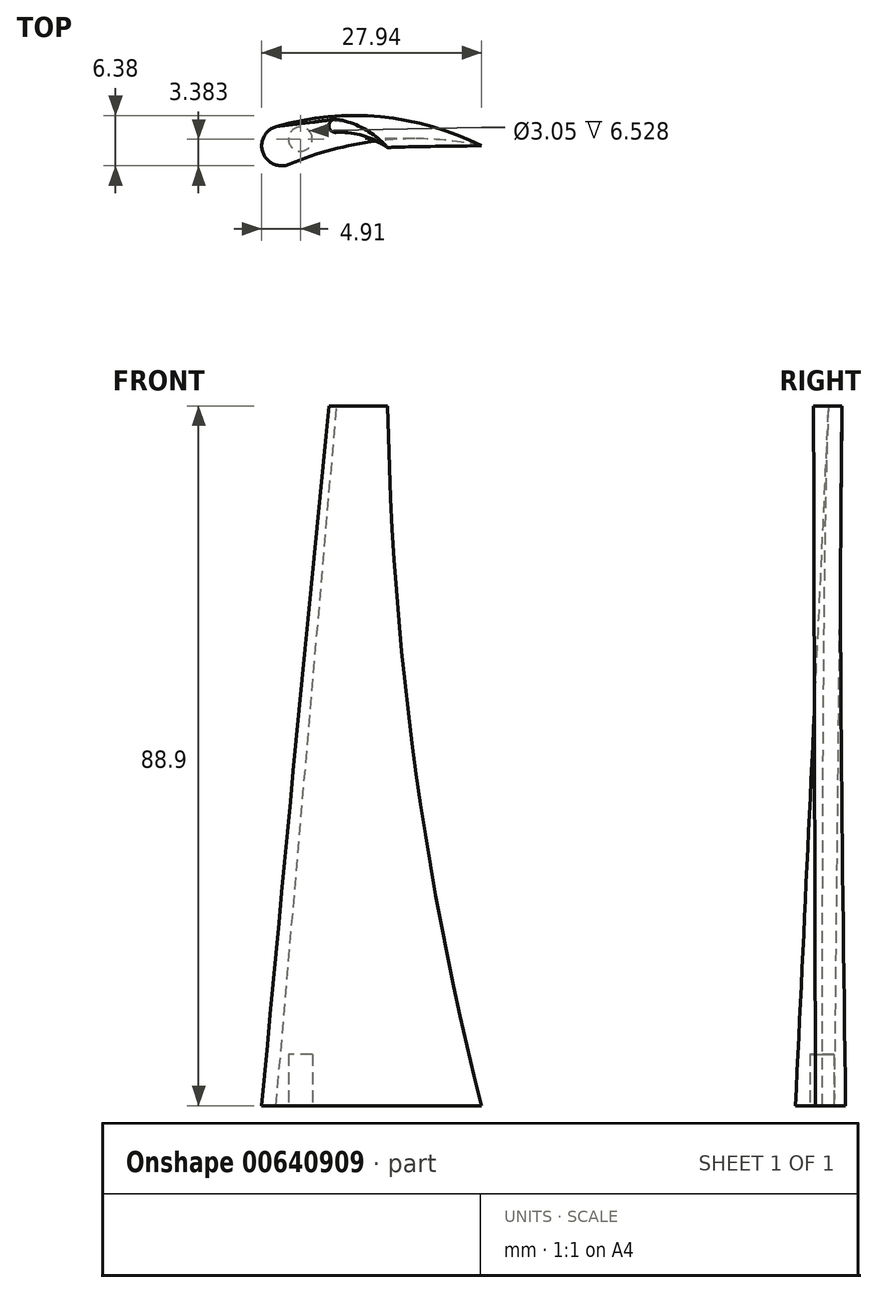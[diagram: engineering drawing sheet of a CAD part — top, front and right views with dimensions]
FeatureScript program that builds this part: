
annotation { "Feature Type Name" : "Feature", "Feature Type Description" : "" }
export const myFeature = defineFeature(function(context is Context, id is Id, definition is map)
    precondition{}
    {
        {
            var Q0;
            Q0=qCreatedBy(makeId("Top.planeOp"),FACE);
            var sketch = newSketch(context, id + "F0", { "sketchPlane" : qUnion([Q0])});
            skLineSegment(sketch, "E0", {"start": v(0, 0) * mm, "end": v(25.4, 0) * mm, "construction": true});
            skArc(sketch, "E1", {"start": v(25.4, 0) * mm, "mid": v(12.58, 3.68) * mm, "end": v(-0.7, 2.44) * mm});
            skArc(sketch, "E2", {"start": v(25.4, 0) * mm, "mid": v(13.02, 0.7) * mm, "end": v(1, -2.34) * mm});
            skArc(sketch, "E3", {"start": v(-0.7, 2.44) * mm, "mid": v(-2.4, -0.85) * mm, "end": v(1, -2.34) * mm});
            skArc(sketch, "E4", {"start": v(1, -2.34) * mm, "mid": v(2.4, 0.85) * mm, "end": v(-0.7, 2.44) * mm, "construction": true});
            skSolve(sketch);
        }
        {
            var Q0;
            Q0=qCreatedBy(makeId("Top.planeOp"),FACE);
            cPlane(context, id + "F1", {"entities" : qUnion([Q0]), "cplaneType" : CPlaneType.OFFSET, "offset" : 88.9 * mm, "width" : 152.4 * mm, "height" : 152.4 * mm});
        }
        {
            var Q0;
            Q0=qCreatedBy(id+"F1.planeOp",FACE);
            var sketch = newSketch(context, id + "F2", { "sketchPlane" : qUnion([Q0])});
            skArc(sketch, "E5", {"start": v(7, 3.37) * mm, "mid": v(6, 2.6) * mm, "end": v(6.9, 1.7) * mm});
            skLineSegment(sketch, "E6", {"start": v(6.85, 2.54) * mm, "end": v(13.46, -0.24) * mm, "construction": true});
            skArc(sketch, "E7", {"start": v(13.46, -0.24) * mm, "mid": v(10.54, 2.12) * mm, "end": v(7, 3.37) * mm});
            skArc(sketch, "E8", {"start": v(13.46, -0.24) * mm, "mid": v(10.34, 1.28) * mm, "end": v(6.9, 1.7) * mm});
            skSolve(sketch);
        }
        {
            var Q0;
            Q0=sQuery(id+"F2.wireOp",VERTEX,"E8.start");
            var Q1;
            Q1=sQuery(id+"F0.wireOp",VERTEX,"E2.start");
            var Q2;
            Q2=sQuery(id+"F0.wireOp",VERTEX,"E3.center");
            cPlane(context, id + "F3", {"entities" : qUnion([Q0, Q1, Q2]), "cplaneType" : CPlaneType.THREE_POINT, "offset" : 25.4 * mm, "width" : 152.4 * mm, "height" : 152.4 * mm});
        }
        {
            var Q0;
            Q0=qCreatedBy(id+"F3.planeOp",FACE);
            var sketch = newSketch(context, id + "F4", { "sketchPlane" : qUnion([Q0])});
            skPoint(sketch, "E9.0", {"position": v(13.46, 88.9) * mm});
            skPoint(sketch, "E10.0", {"position": v(25.4, 0) * mm});
            skArc(sketch, "E11", {"start": v(13.46, 88.9) * mm, "mid": v(16.82, 44.1) * mm, "end": v(25.4, 0) * mm});
            skLineSegment(sketch, "E12.0", {"start": v(6.85, 88.9) * mm, "end": v(13.46, 88.9) * mm, "construction": true});
            skSolve(sketch);
        }
        {
            var Q0;
            Q0=makeQuery(id+"F0.imprint","IMPRINT",FACE,{"disambiguationData":[TD([[makeQuery(id+"F0.imprint","IMPRINT",EDGE,{"derivedFrom":sQuery(id+"F0.wireOp",EDGE,"E1")}),1.0]])]});
            var Q1;
            {var subQ0=sQuery(id+"F2.wireOp",EDGE,"E5");Q1=makeQuery(id+"F2.imprint","IMPRINT",FACE,{"disambiguationData":[TD([[makeQuery(id+"F2.imprint","IMPRINT",EDGE,{"derivedFrom":subQ0}),1.0]])]});}
            var Q2;
            Q2=sQuery(id+"F4.wireOp",EDGE,"E11");
            var Q3;
            Q3=sQuery(id+"F0.wireOp",VERTEX,"E2.start");
            var Q4;
            Q4=sQuery(id+"F2.wireOp",VERTEX,"E8.start");
            loft(context, id + "F5", {"addGuides" : true, "sheetProfilesArray" : [{ "sheetProfileEntities" : qUnion([Q0]) }, { "sheetProfileEntities" : qUnion([Q1]) }], "guidesArray" : [{ "guideEntities" : qUnion([Q2]), "guideDerivativeType" : LoftGuideDerivativeType.DEFAULT, "guideDerivativeMagnitude" : 1 }], "matchConnections" : true, "connections" : [{ "connectionEntities" : qUnion([Q3, Q4]), "connectionEdgeQueries" : qUnion([]), "connectionEdgeParameters" : [] }]});
        }
        {
            var Q0;
            Q0=makeQuery(id+"F0.imprint","IMPRINT",FACE,{"disambiguationData":[TD([[makeQuery(id+"F0.imprint","IMPRINT",EDGE,{"derivedFrom":sQuery(id+"F0.wireOp",EDGE,"E1")}),1.0]])]});
            var sketch = newSketch(context, id + "F6", { "sketchPlane" : qUnion([Q0])});
            skCircle(sketch, "E13", {"center": v(2.37, 0.84) * mm, "radius": 1.52 * mm});
            skSolve(sketch);
        }
        {
            var Q0;
            Q0=makeQuery(id+"F6.imprint","IMPRINT",FACE,{"disambiguationData":[TD([[makeQuery(id+"F6.imprint","IMPRINT",EDGE,{"derivedFrom":sQuery(id+"F6.wireOp",EDGE,"E13")}),1.0]])]});
            extrude(context, id + "F7", {"entities" : qUnion([Q0]), "operationType" : NewBodyOperationType.REMOVE, "depth" : 6.53 * mm, "offsetDistance" : 25.4 * mm});
        }
    });
